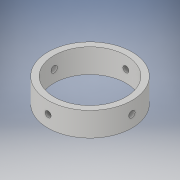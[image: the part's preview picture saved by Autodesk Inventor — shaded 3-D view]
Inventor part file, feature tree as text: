
AUTODESK INVENTOR PART (.ipt)
format: ipt  version: 2017 SP1 (Build 210196100, 196)  size: 129,024 bytes
history: native  units: in
note: dims shown in document units (in); Inventor stores cm internally (conversion verified against a paired STEP export)
features: sketch x3, plane x2, hole x2, extrude x1
ambient origin geometry x8: Origin, YZ Plane, XZ Plane, XY Plane, X Axis, Y Axis, Z Axis, Center Point
bodies: Solid1 (feature_tree)
feature tree (8):
  extrude  "Extrusion1"  Depth=3.5in
  plane  "Work Plane1"
  hole  "Hole1"  [1 undecoded]
  plane  "Work Plane2"
  hole  "Hole2"  [1 undecoded]
  sketch  "Sketch1"  dims[d0=3.0in d1=3.5in]
  sketch  "Sketch2"  dims[d2=1.0in d3=0.0in]
  sketch  "Sketch3"  dims[d4=1.75in d5=0.25in d6=0.75in d7=0.375in d8=0.25in d9=0.5635in d10=1.0in d11=0.8108in d12=1.75in d13=0.266in d14=0.75in d15=0.507in d16=0.25in d17=0.5635in d18=1.0in d19=0.8108in]
note: 2 required parameter values undecoded (feature->parameter linkage not recoverable at this tier; creation-order binding heuristic only, values carry confidence <= 0.55)
